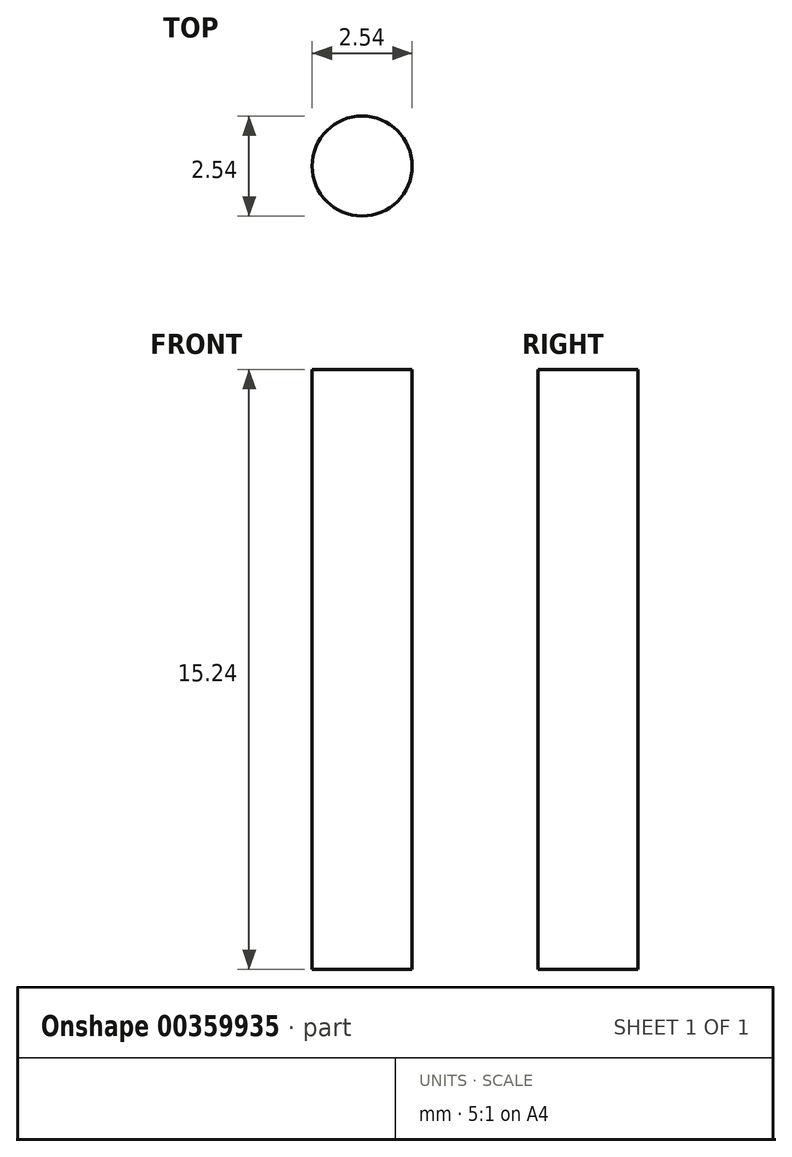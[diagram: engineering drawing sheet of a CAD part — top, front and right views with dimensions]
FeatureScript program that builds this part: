
annotation { "Feature Type Name" : "Feature", "Feature Type Description" : "" }
export const myFeature = defineFeature(function(context is Context, id is Id, definition is map)
    precondition{}
    {
        {
            var Q0;
            Q0=qCreatedBy(makeId("Top.planeOp"),FACE);
            var sketch = newSketch(context, id + "F0", { "sketchPlane" : qUnion([Q0])});
            skPoint(sketch, "E0", {"position": v(1.27, 0) * mm});
            skCircle(sketch, "E1", {"center": v(0, 0) * mm, "radius": 1.27 * mm});
            skSolve(sketch);
        }
        {
            var Q0;
            Q0 = qSketchRegion(id + "F0", true);
            extrude(context, id + "F1", {"entities" : qUnion([Q0]), "depth" : 15.24 * mm});
        }
    });
